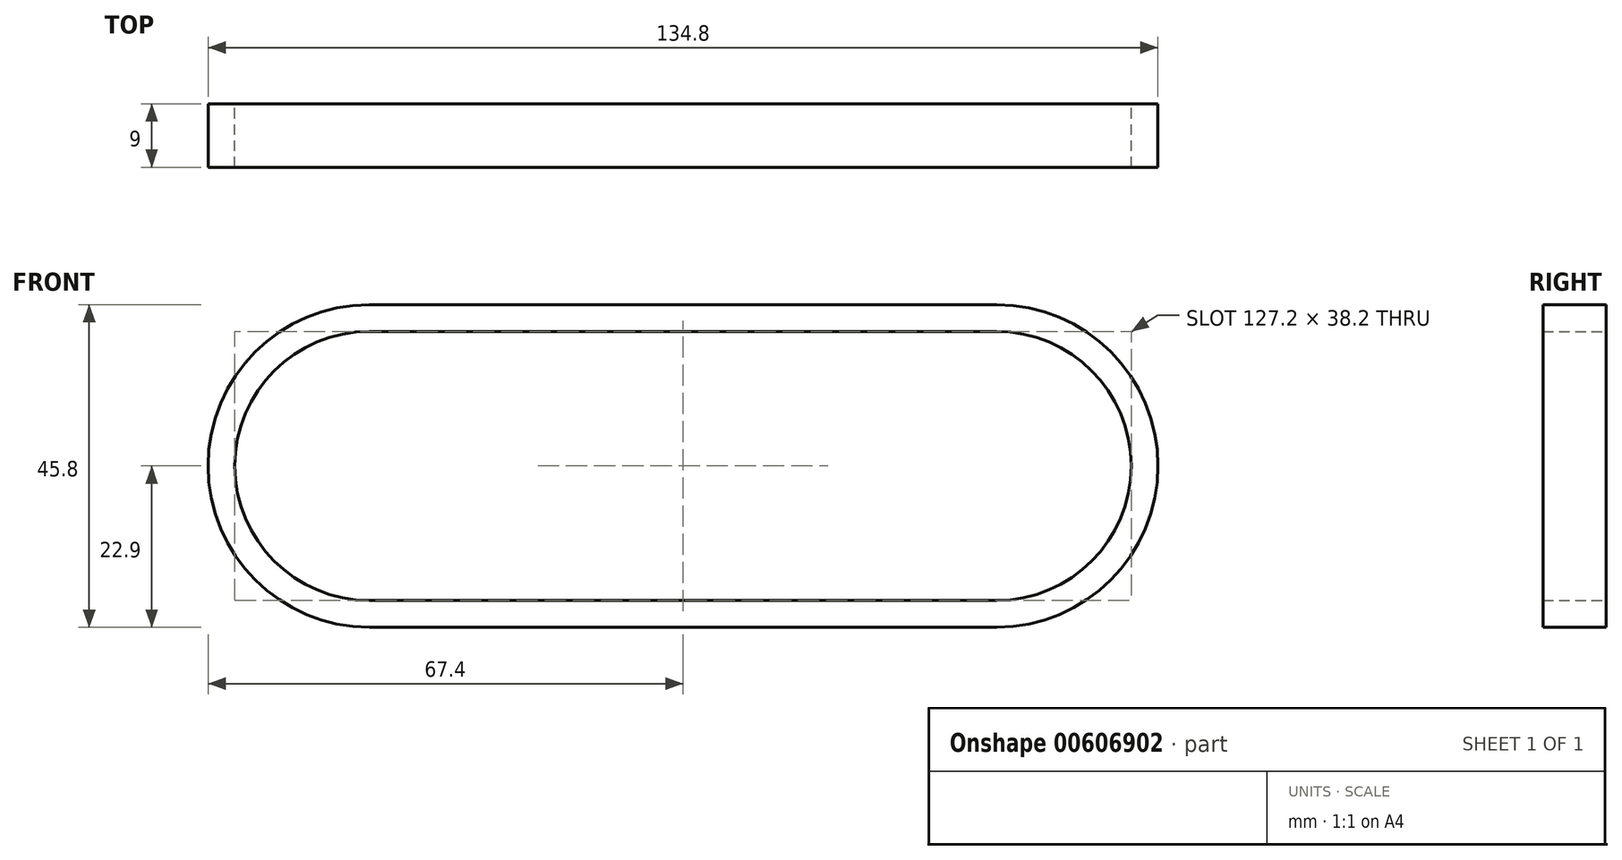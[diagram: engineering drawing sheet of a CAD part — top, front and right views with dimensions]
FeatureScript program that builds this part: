
annotation { "Feature Type Name" : "Feature", "Feature Type Description" : "" }
export const myFeature = defineFeature(function(context is Context, id is Id, definition is map)
    precondition{}
    {
        {
            var Q0;
            Q0=qCreatedBy(makeId("Front.planeOp"),FACE);
            var sketch = newSketch(context, id + "F0", { "sketchPlane" : qUnion([Q0]) });
            skArc(sketch, "E0", {"start": v(0, 21) * mm, "mid": v(-21, 0) * mm, "end": v(0, -21) * mm});
            skArc(sketch, "E1", {"start": v(89, -21) * mm, "mid": v(110, 0) * mm, "end": v(89, 21) * mm});
            skLineSegment(sketch, "E2", {"start": v(0, 21) * mm, "end": v(89, 21) * mm});
            skLineSegment(sketch, "E3", {"start": v(0, -21) * mm, "end": v(89, -21) * mm});
            skSolve(sketch);
        }
        {
            var Q0;
            Q0=qCreatedBy(makeId("Right.planeOp"),FACE);
            var sketch = newSketch(context, id + "F1", { "sketchPlane" : qUnion([Q0]) });
            skPoint(sketch, "E4.0", {"position": v(0, 21) * mm});
            skLineSegment(sketch, "E5.bottom", {"start": v(-4.5, 22.9) * mm, "end": v(4.5, 22.9) * mm});
            skLineSegment(sketch, "E5.top", {"start": v(-4.5, 19.1) * mm, "end": v(4.5, 19.1) * mm});
            skLineSegment(sketch, "E5.left", {"start": v(-4.5, 22.9) * mm, "end": v(-4.5, 19.1) * mm});
            skLineSegment(sketch, "E5.right", {"start": v(4.5, 22.9) * mm, "end": v(4.5, 19.1) * mm});
            skSolve(sketch);
        }
        {
            var Q0;
            Q0=makeQuery(id+"F1.imprint","IMPRINT",FACE,{"disambiguationData":[TD([[makeQuery(id+"F1.imprint","IMPRINT",EDGE,{"derivedFrom":sQuery(id+"F1.wireOp",EDGE,"E5.bottom")}),-1.0]])]});
            var Q1;
            Q1=sQuery(id+"F0.wireOp",EDGE,"E0");
            var Q2;
            Q2=sQuery(id+"F0.wireOp",EDGE,"E3");
            var Q3;
            Q3=sQuery(id+"F0.wireOp",EDGE,"E1");
            var Q4;
            Q4=sQuery(id+"F0.wireOp",EDGE,"E2");
            sweep(context, id + "F2", {"profiles" : qUnion([Q0]), "path" : qUnion([Q1, Q2, Q3, Q4])});
        }
    });
